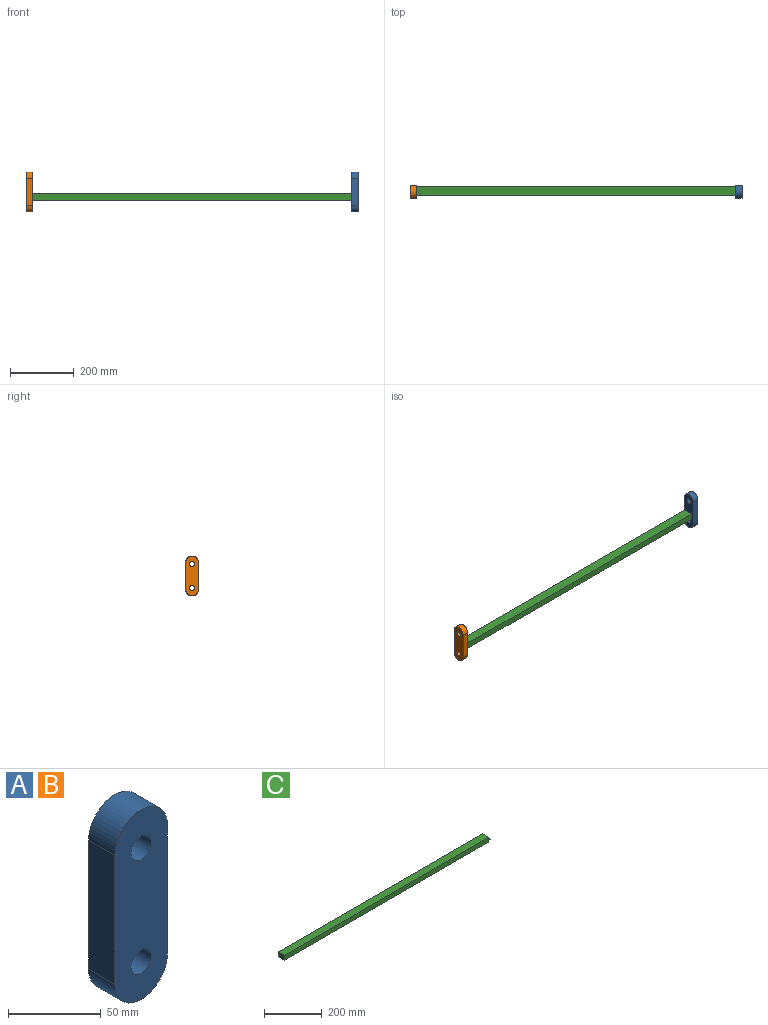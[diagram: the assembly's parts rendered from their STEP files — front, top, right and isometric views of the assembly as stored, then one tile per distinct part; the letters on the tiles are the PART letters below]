
ASSEMBLY  parts=3 mates=1
PART A: 10 faces, bbox 40x20x125 mm
  f0: plane 85x20mm, normal (1,0,0), area 1700mm2, adj f1,f5,f6,f7
  f1: cylinder r=20mm len=40mm, axis (0,1,0), area 1256.6mm2, adj f0,f2,f6,f7
  f2: plane 85x20mm, normal (-1,0,0), area 1700mm2, adj f1,f5,f6,f7
  f3: cylinder r=7.75mm len=20mm, axis (0,1,0), area 973.9mm2, adj f6,f7
  f4: cylinder r=7.75mm len=20mm, axis (0,1,0), area 973.9mm2, adj f6,f7
  f5: cylinder r=20mm len=40mm, axis (0,1,0), area 1256.6mm2, adj f0,f2,f6,f7
  f6: plane 125x40mm, normal (0,-1,0), area 4279.3mm2, adj f0,f1,f2,f3,f4,f5
  f7: plane 125x40mm, normal (0,1,0), area 4259.6mm2, adj f0,f1,f2,f3,f4,f5,f8
  f8: cylinder r=2.5mm len=5mm, axis (0,1,0), area 78.5mm2, adj f7,f9
  f9: plane 5x5mm, normal (0,1,0), area 19.6mm2, adj f8
PART B: same geometry as A
PART C: 11 faces, bbox 1012x30.7x20 mm
  f0: plane 1002x30mm, normal (0,0,1), area 30060mm2, adj f1,f3,f4,f5
  f1: plane 30x20mm, normal (-1,0,0), area 581.1mm2, adj f0,f2,f4,f5,f6
  f2: plane 1002x30mm, normal (0,0,-1), area 30060mm2, adj f1,f3,f4,f5
  f3: plane 30x20mm, normal (1,0,0), area 582mm2, adj f0,f2,f4,f5,f9
  f4: plane 1002x20mm, normal (0,-1,0), area 20040mm2, adj f0,f1,f2,f3,f8
  f5: plane 1002x20mm, normal (0,1,0), area 20040mm2, adj f0,f1,f2,f3
  f6: cylinder r=2.45mm len=5mm, axis (1,0,0), area 77mm2, adj f1,f7
  f7: plane 4.9x4.9mm, normal (-1,0,0), area 18.9mm2, adj f6
  f8: plane 3.43x0.68mm, normal (-1,0,0), area 1.6mm2, adj f4,f9
  f9: cylinder r=2.5mm len=5mm, axis (-1,0,0), area 78.5mm2, adj f3,f8,f10
  f10: plane 5x5mm, normal (1,0,0), area 19.6mm2, adj f9
PLACE A rot(axis=(0,0,1),90deg) t=(-651.46,-53.24,-43.89)mm
PLACE B rot(axis=(0,0,-1),90deg) t=(-1653.46,-53.92,-43.89)mm
PLACE C rot(axis=(0,1,0),180deg) t=(-1152.46,-35.74,-27.31)mm
MATE fastened C.f6 <-> A.f8  axis (1,0,0) through (-651.46,-43.24,-59.89)mm
